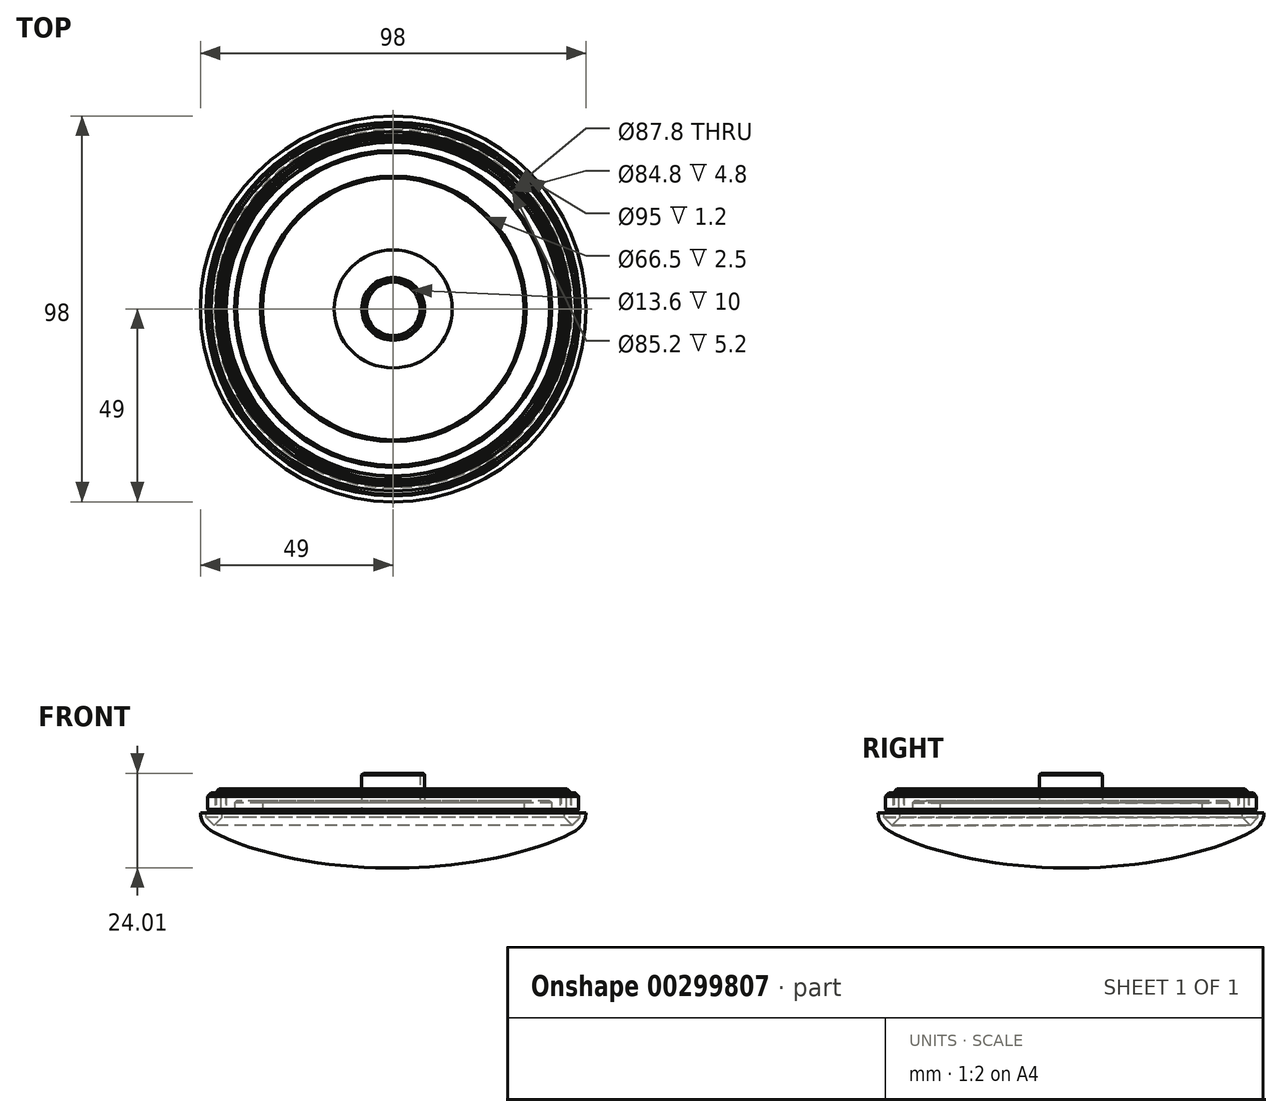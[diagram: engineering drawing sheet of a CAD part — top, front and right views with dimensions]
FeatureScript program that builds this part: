
annotation { "Feature Type Name" : "Feature", "Feature Type Description" : "" }
export const myFeature = defineFeature(function(context is Context, id is Id, definition is map)
    precondition{}
    {
        {
            var Q0;
            Q0=qCreatedBy(makeId("Top.planeOp"),FACE);
            var sketch = newSketch(context, id + "F0", { "sketchPlane" : qUnion([Q0])});
            skCircle(sketch, "E0", {"center": v(0, 0) * mm, "radius": 8 * mm});
            skCircle(sketch, "E1", {"center": v(0, 0) * mm, "radius": 6.8 * mm});
            skSolve(sketch);
        }
        {
            var Q0;
            Q0 = qSketchRegion(id + "F0", true);
            extrude(context, id + "F1", {"entities" : qUnion([Q0]), "depth" : 10 * mm, "offsetDistance" : 25 * mm});
        }
        {
            var Q0;
            Q0=qCreatedBy(makeId("Top.planeOp"),FACE);
            var sketch = newSketch(context, id + "F2", { "sketchPlane" : qUnion([Q0])});
            skCircle(sketch, "E2", {"center": v(0, 0) * mm, "radius": 15 * mm});
            skCircle(sketch, "E3", {"center": v(0, 0) * mm, "radius": 6.8 * mm});
            skSolve(sketch);
        }
        {
            var Q0;
            Q0 = qSketchRegion(id + "F2", true);
            extrude(context, id + "F3", {"entities" : qUnion([Q0]), "operationType" : NewBodyOperationType.ADD, "depth" : 1 * mm, "offsetDistance" : 25 * mm});
        }
        {
            var Q0;
            Q0=makeQuery(id+"F1.opExtrude","CAP_EDGE",EDGE,{"disambiguationData":[OSD([sQuery(id+"F0.wireOp",EDGE,"E0")])],"isStart":false});
            chamfer(context, id + "F4", {"entities" : qUnion([Q0]), "width" : 0.4 * mm, "tangentPropagation" : true});
        }
        {
            var Q0;
            Q0=qCreatedBy(makeId("Top.planeOp"),FACE);
            var sketch = newSketch(context, id + "F5", { "sketchPlane" : qUnion([Q0])});
            skCircle(sketch, "E4", {"center": v(0, 0) * mm, "radius": 45 * mm});
            skCircle(sketch, "E5", {"center": v(0, 0) * mm, "radius": 42.6 * mm});
            skSolve(sketch);
        }
        {
            var Q0;
            Q0 = qSketchRegion(id + "F5", true);
            extrude(context, id + "F6", {"entities" : qUnion([Q0]), "depth" : 6 * mm, "offsetDistance" : 25 * mm});
        }
        {
            var Q0;
            Q0=makeQuery(id+"F6.opExtrude","CAP_FACE",FACE,{"disambiguationData":[OSD([sQuery(id+"F5.wireOp",EDGE,"E4"),sQuery(id+"F5.wireOp",EDGE,"E5")])],"isStart":false});
            chamfer(context, id + "F7", {"entities" : qUnion([Q0]), "width" : 0.8 * mm, "tangentPropagation" : true});
        }
        {
            var Q0;
            Q0=qCreatedBy(makeId("Top.planeOp"),FACE);
            var sketch = newSketch(context, id + "F8", { "sketchPlane" : qUnion([Q0])});
            skCircle(sketch, "E6", {"center": v(0, 0) * mm, "radius": 45.2 * mm});
            skCircle(sketch, "E7", {"center": v(0, 0) * mm, "radius": 42.4 * mm});
            skSolve(sketch);
        }
        {
            var Q0;
            Q0 = qSketchRegion(id + "F8", true);
            extrude(context, id + "F9", {"entities" : qUnion([Q0]), "depth" : 6 * mm, "offsetDistance" : 25 * mm});
        }
        {
            var Q0;
            Q0=makeQuery(id+"F9.opExtrude","CAP_FACE",FACE,{"disambiguationData":[OSD([sQuery(id+"F8.wireOp",EDGE,"E6"),sQuery(id+"F8.wireOp",EDGE,"E7")])],"isStart":false});
            chamfer(context, id + "F10", {"entities" : qUnion([Q0]), "width" : 1.2 * mm, "tangentPropagation" : true});
        }
        {
            var Q0;
            Q0=qCreatedBy(makeId("Top.planeOp"),FACE);
            var sketch = newSketch(context, id + "F11", { "sketchPlane" : qUnion([Q0])});
            skCircle(sketch, "E8", {"center": v(0, 0) * mm, "radius": 47.5 * mm});
            skSolve(sketch);
        }
        {
            var Q0;
            Q0=qCreatedBy(makeId("Front.planeOp"),FACE);
            var sketch = newSketch(context, id + "F12", { "sketchPlane" : qUnion([Q0])});
            skLineSegment(sketch, "E9", {"start": v(0, 0) * mm, "end": v(0, -14) * mm});
            skLineSegment(sketch, "E10", {"start": v(0, 0) * mm, "end": v(43.5, 0) * mm});
            skFitSpline(sketch, "E11", {"points": [v(49, 0) * mm, v(48.03, -3.01) * mm, v(45.87, -4.84) * mm, v(35.93, -8.93) * mm, v(16.67, -13.05) * mm, v(0, -14) * mm], "startDerivative": vector(0.4, -33.8) * mm, "endDerivative": vector(-56.73, 0.72) * mm});
            skLineSegment(sketch, "E12", {"start": v(47.5, 0) * mm, "end": v(47.5, -1.2) * mm});
            skLineSegment(sketch, "E13", {"start": v(47.5, -1.2) * mm, "end": v(45.5, -3.2) * mm});
            skLineSegment(sketch, "E14", {"start": v(45.5, -3.2) * mm, "end": v(45.5, -1.2) * mm});
            skLineSegment(sketch, "E15.MirrorCS", {"start": v(43.5, -1.2) * mm, "end": v(45.5, -3.2) * mm});
            skLineSegment(sketch, "E16.MirrorCS", {"start": v(43.5, 0) * mm, "end": v(43.5, -1.2) * mm});
            skLineSegment(sketch, "E17.trimOffspring", {"start": v(47.5, 0) * mm, "end": v(49, 0) * mm});
            skSolve(sketch);
        }
        {
            var Q0;
            Q0 = qSketchRegion(id + "F12", true);
            var Q1;
            Q1=sQuery(id+"F12.wireOp",EDGE,"E9");
            revolve(context, id + "F13", {"surfaceOperationType" : NewSurfaceOperationType.NEW, "entities" : qUnion([Q0]), "axis" : qUnion([Q1]), "revolveType" : RevolveType.FULL});
        }
        {
            var Q0;
            Q0=makeQuery(id+"F11.imprint","IMPRINT",FACE,{"disambiguationData":[TD([[makeQuery(id+"F11.imprint","IMPRINT",EDGE,{"derivedFrom":sQuery(id+"F11.wireOp",EDGE,"E8")}),1.0]])]});
            var sketch = newSketch(context, id + "F14", { "sketchPlane" : qUnion([Q0])});
            skCircle(sketch, "E18", {"center": v(0, 0) * mm, "radius": 47.1 * mm});
            skCircle(sketch, "E19", {"center": v(0, 0) * mm, "radius": 43.9 * mm});
            skSolve(sketch);
        }
        {
            var Q0;
            Q0 = qSketchRegion(id + "F14", true);
            extrude(context, id + "F15", {"entities" : qUnion([Q0]), "depth" : 5 * mm, "offsetDistance" : 25 * mm});
        }
        {
            var Q0;
            Q0=makeQuery(id+"F15.opExtrude","CAP_FACE",FACE,{"disambiguationData":[OSD([sQuery(id+"F14.wireOp",EDGE,"E18"),sQuery(id+"F14.wireOp",EDGE,"E19")])],"isStart":false});
            var Q1;
            Q1=makeQuery(id+"F15.opExtrude","CAP_FACE",FACE,{"disambiguationData":[OSD([sQuery(id+"F14.wireOp",EDGE,"E18"),sQuery(id+"F14.wireOp",EDGE,"E19")])],"isStart":true});
            chamfer(context, id + "F16", {"entities" : qUnion([Q0, Q1]), "width" : 0.8 * mm, "tangentPropagation" : true});
        }
        {
            var Q0;
            Q0=makeQuery(id+"F11.imprint","IMPRINT",FACE,{"disambiguationData":[TD([[makeQuery(id+"F11.imprint","IMPRINT",EDGE,{"derivedFrom":sQuery(id+"F11.wireOp",EDGE,"E8")}),1.0]])]});
            var sketch = newSketch(context, id + "F17", { "sketchPlane" : qUnion([Q0])});
            skCircle(sketch, "E20", {"center": v(0, 0) * mm, "radius": 33.25 * mm});
            skCircle(sketch, "E21", {"center": v(0, 0) * mm, "radius": 40.25 * mm});
            skSolve(sketch);
        }
        {
            var Q0;
            Q0 = qSketchRegion(id + "F17", true);
            extrude(context, id + "F18", {"entities" : qUnion([Q0]), "operationType" : NewBodyOperationType.ADD, "depth" : 3 * mm, "offsetDistance" : 25 * mm});
        }
        {
            var Q0;
            Q0=makeQuery(id+"F18.opExtrude","CAP_FACE",FACE,{"disambiguationData":[OSD([sQuery(id+"F17.wireOp",EDGE,"E20"),sQuery(id+"F17.wireOp",EDGE,"E21")])],"isStart":false});
            chamfer(context, id + "F19", {"entities" : qUnion([Q0]), "width" : 0.5 * mm, "tangentPropagation" : true});
        }
    });
